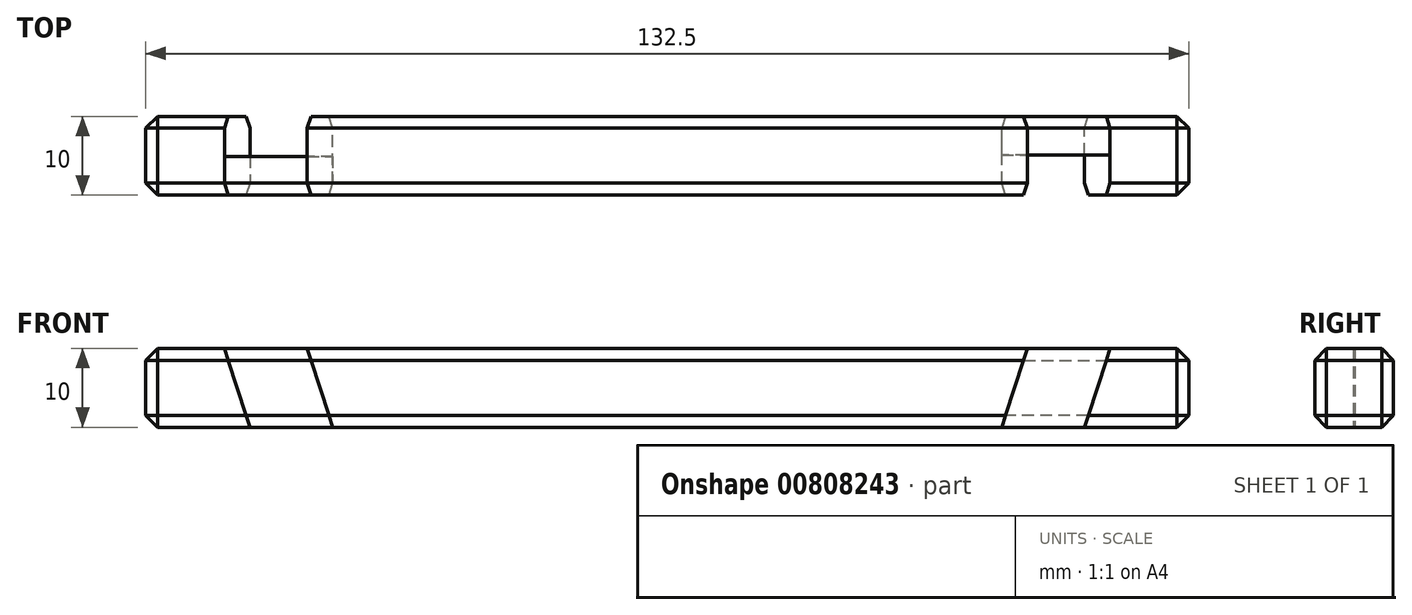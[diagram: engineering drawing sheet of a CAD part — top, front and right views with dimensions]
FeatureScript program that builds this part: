
annotation { "Feature Type Name" : "Feature", "Feature Type Description" : "" }
export const myFeature = defineFeature(function(context is Context, id is Id, definition is map)
    precondition{}
    {
        {
            var Q0;
            Q0=qCreatedBy(makeId("Front.planeOp"),FACE);
            var sketch = newSketch(context, id + "F0", { "sketchPlane" : qUnion([Q0])});
            skLineSegment(sketch, "E0", {"start": v(-60.02, 0) * mm, "end": v(-60.02, 10) * mm});
            skLineSegment(sketch, "E1", {"start": v(-60.02, 10) * mm, "end": v(-50.02, 10) * mm});
            skLineSegment(sketch, "E2", {"start": v(-50.02, 10) * mm, "end": v(-46.77, 0) * mm});
            skLineSegment(sketch, "E3", {"start": v(-46.77, 0) * mm, "end": v(-60.02, 0) * mm});
            skLineSegment(sketch, "E4", {"start": v(-39.5, 10) * mm, "end": v(-36.26, 0) * mm});
            skLineSegment(sketch, "E5", {"start": v(-36.26, 0) * mm, "end": v(48.71, 0) * mm});
            skLineSegment(sketch, "E6", {"start": v(48.71, 0) * mm, "end": v(51.96, 10) * mm});
            skLineSegment(sketch, "E7", {"start": v(51.96, 10) * mm, "end": v(-39.5, 10) * mm});
            skLineSegment(sketch, "E8", {"start": v(-50.02, 10) * mm, "end": v(-39.5, 10) * mm});
            skLineSegment(sketch, "E9", {"start": v(-46.77, 0) * mm, "end": v(-36.26, 0) * mm});
            skLineSegment(sketch, "E10", {"start": v(51.96, 10) * mm, "end": v(62.48, 10) * mm});
            skLineSegment(sketch, "E11", {"start": v(62.48, 10) * mm, "end": v(59.23, 0) * mm});
            skLineSegment(sketch, "E12", {"start": v(59.23, 0) * mm, "end": v(48.71, 0) * mm});
            skLineSegment(sketch, "E13", {"start": v(62.48, 10) * mm, "end": v(72.48, 10) * mm});
            skLineSegment(sketch, "E14", {"start": v(72.48, 10) * mm, "end": v(72.48, 0) * mm});
            skLineSegment(sketch, "E15", {"start": v(72.48, 0) * mm, "end": v(59.23, 0) * mm});
            skSolve(sketch);
        }
        {
            var Q0;
            Q0=makeQuery(id+"F0.imprint","IMPRINT",FACE,{"disambiguationData":[TD([[makeQuery(id+"F0.imprint","IMPRINT",EDGE,{"derivedFrom":sQuery(id+"F0.wireOp",EDGE,"E0")}),-1.0]])]});
            var Q1;
            Q1=makeQuery(id+"F0.imprint","IMPRINT",FACE,{"disambiguationData":[TD([[makeQuery(id+"F0.imprint","IMPRINT",EDGE,{"derivedFrom":sQuery(id+"F0.wireOp",EDGE,"E4")}),1.0]])]});
            var Q2;
            Q2=makeQuery(id+"F0.imprint","IMPRINT",FACE,{"disambiguationData":[TD([[makeQuery(id+"F0.imprint","IMPRINT",EDGE,{"derivedFrom":sQuery(id+"F0.wireOp",EDGE,"E11")}),1.0]])]});
            extrude(context, id + "F1", {"entities" : qUnion([Q0, Q1, Q2]), "depth" : 10 * mm, "offsetDistance" : 25 * mm});
        }
        {
            var Q0;
            Q0=makeQuery(id+"F1.opExtrude","CAP_FACE",FACE,{"disambiguationData":[OSD([sQuery(id+"F0.wireOp",EDGE,"E11"),sQuery(id+"F0.wireOp",EDGE,"E13"),sQuery(id+"F0.wireOp",EDGE,"E14"),sQuery(id+"F0.wireOp",EDGE,"E15")])],"isStart":true});
            var sketch = newSketch(context, id + "F2", { "sketchPlane" : qUnion([Q0])});
            skLineSegment(sketch, "E16", {"start": v(-62.48, 10) * mm, "end": v(-51.96, 10) * mm});
            skLineSegment(sketch, "E17", {"start": v(-51.96, 10) * mm, "end": v(-48.71, 0) * mm});
            skLineSegment(sketch, "E18", {"start": v(-48.71, 0) * mm, "end": v(-59.23, 0) * mm});
            skLineSegment(sketch, "E19", {"start": v(-59.23, 0) * mm, "end": v(-62.48, 10) * mm});
            skSolve(sketch);
        }
        {
            var Q0;
            Q0=makeQuery(id+"F2.imprint","IMPRINT",FACE,{"disambiguationData":[TD([[makeQuery(id+"F2.imprint","IMPRINT",EDGE,{"derivedFrom":sQuery(id+"F2.wireOp",EDGE,"E16")}),-1.0]])]});
            extrude(context, id + "F3", {"entities" : qUnion([Q0]), "oppositeDirection" : true, "depth" : 4.9 * mm, "offsetDistance" : 25 * mm});
        }
        {
            var Q0;
            Q0=makeQuery(id+"F1.opExtrude","CAP_FACE",FACE,{"disambiguationData":[OSD([sQuery(id+"F0.wireOp",EDGE,"E0"),sQuery(id+"F0.wireOp",EDGE,"E1"),sQuery(id+"F0.wireOp",EDGE,"E2"),sQuery(id+"F0.wireOp",EDGE,"E3")])],"isStart":false});
            var sketch = newSketch(context, id + "F4", { "sketchPlane" : qUnion([Q0])});
            skLineSegment(sketch, "E20", {"start": v(-50.02, 10) * mm, "end": v(-39.5, 10) * mm});
            skLineSegment(sketch, "E21", {"start": v(-39.5, 10) * mm, "end": v(-36.26, 0) * mm});
            skLineSegment(sketch, "E22", {"start": v(-36.26, 0) * mm, "end": v(-46.77, 0) * mm});
            skLineSegment(sketch, "E23", {"start": v(-46.77, 0) * mm, "end": v(-50.02, 10) * mm});
            skSolve(sketch);
        }
        {
            var Q0;
            Q0=makeQuery(id+"F4.imprint","IMPRINT",FACE,{"disambiguationData":[TD([[makeQuery(id+"F4.imprint","IMPRINT",EDGE,{"derivedFrom":sQuery(id+"F4.wireOp",EDGE,"E20")}),-1.0]])]});
            extrude(context, id + "F5", {"entities" : qUnion([Q0]), "oppositeDirection" : true, "depth" : 4.9 * mm, "offsetDistance" : 25 * mm});
        }
        {
            var Q0;
            Q0=makeQuery(id+"F1.opExtrude","SWEPT_FACE",FACE,{"disambiguationData":[OSD([sQuery(id+"F0.wireOp",EDGE,"E0")])]});
            var Q1;
            Q1=makeQuery(id+"F1.opExtrude","CAP_EDGE",EDGE,{"disambiguationData":[OSD([sQuery(id+"F0.wireOp",EDGE,"E1")])],"isStart":true});
            var Q2;
            Q2=makeQuery(id+"F1.opExtrude","CAP_EDGE",EDGE,{"disambiguationData":[OSD([sQuery(id+"F0.wireOp",EDGE,"E3")])],"isStart":true});
            var Q3;
            Q3=makeQuery(id+"F1.opExtrude","CAP_EDGE",EDGE,{"disambiguationData":[OSD([sQuery(id+"F0.wireOp",EDGE,"E3")])],"isStart":false});
            var Q4;
            Q4=makeQuery(id+"F1.opExtrude","CAP_EDGE",EDGE,{"disambiguationData":[OSD([sQuery(id+"F0.wireOp",EDGE,"E1")])],"isStart":false});
            var Q5;
            Q5=makeQuery(id+"F5.opExtrude","CAP_EDGE",EDGE,{"disambiguationData":[OSD([sQuery(id+"F4.wireOp",EDGE,"E22")])],"isStart":true});
            var Q6;
            Q6=makeQuery(id+"F1.opExtrude","CAP_EDGE",EDGE,{"disambiguationData":[OSD([sQuery(id+"F0.wireOp",EDGE,"E5")])],"isStart":false});
            var Q7;
            Q7=makeQuery(id+"F1.opExtrude","CAP_EDGE",EDGE,{"disambiguationData":[OSD([sQuery(id+"F0.wireOp",EDGE,"E5")])],"isStart":true});
            var Q8;
            Q8=makeQuery(id+"F5.opExtrude","CAP_EDGE",EDGE,{"disambiguationData":[OSD([sQuery(id+"F4.wireOp",EDGE,"E20")])],"isStart":true});
            var Q9;
            Q9=makeQuery(id+"F1.opExtrude","CAP_EDGE",EDGE,{"disambiguationData":[OSD([sQuery(id+"F0.wireOp",EDGE,"E7")])],"isStart":false});
            var Q10;
            Q10=makeQuery(id+"F1.opExtrude","CAP_EDGE",EDGE,{"disambiguationData":[OSD([sQuery(id+"F0.wireOp",EDGE,"E15")])],"isStart":false});
            var Q11;
            Q11=makeQuery(id+"F1.opExtrude","CAP_EDGE",EDGE,{"disambiguationData":[OSD([sQuery(id+"F0.wireOp",EDGE,"E13")])],"isStart":false});
            var Q12;
            Q12=makeQuery(id+"F1.opExtrude","CAP_EDGE",EDGE,{"disambiguationData":[OSD([sQuery(id+"F0.wireOp",EDGE,"E14")])],"isStart":false});
            var Q13;
            Q13=makeQuery(id+"F1.opExtrude","SWEPT_EDGE",EDGE,{"disambiguationData":[OSD([sQuery(id+"F0.wireOp",EDGE,"E14"),sQuery(id+"F0.wireOp",EDGE,"E15")])]});
            var Q14;
            Q14=makeQuery(id+"F1.opExtrude","CAP_EDGE",EDGE,{"disambiguationData":[OSD([sQuery(id+"F0.wireOp",EDGE,"E14")])],"isStart":true});
            var Q15;
            Q15=makeQuery(id+"F1.opExtrude","SWEPT_EDGE",EDGE,{"disambiguationData":[OSD([sQuery(id+"F0.wireOp",EDGE,"E13"),sQuery(id+"F0.wireOp",EDGE,"E14")])]});
            var Q16;
            Q16=makeQuery(id+"F1.opExtrude","CAP_EDGE",EDGE,{"disambiguationData":[OSD([sQuery(id+"F0.wireOp",EDGE,"E13")])],"isStart":true});
            var Q17;
            Q17=makeQuery(id+"F1.opExtrude","CAP_EDGE",EDGE,{"disambiguationData":[OSD([sQuery(id+"F0.wireOp",EDGE,"E15")])],"isStart":true});
            var Q18;
            Q18=makeQuery(id+"F1.opExtrude","CAP_EDGE",EDGE,{"disambiguationData":[OSD([sQuery(id+"F0.wireOp",EDGE,"E7")])],"isStart":true});
            var Q19;
            Q19=makeQuery(id+"F3.opExtrude","CAP_EDGE",EDGE,{"disambiguationData":[OSD([sQuery(id+"F2.wireOp",EDGE,"E16")])],"isStart":true});
            var Q20;
            Q20=makeQuery(id+"F3.opExtrude","CAP_EDGE",EDGE,{"disambiguationData":[OSD([sQuery(id+"F2.wireOp",EDGE,"E18")])],"isStart":true});
            chamfer(context, id + "F6", {"entities" : qUnion([Q0, Q1, Q2, Q3, Q4, Q5, Q6, Q7, Q8, Q9, Q10, Q11, Q12, Q13, Q14, Q15, Q16, Q17, Q18, Q19, Q20]), "width" : 1.5 * mm, "tangentPropagation" : true});
        }
    });
